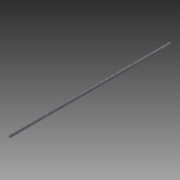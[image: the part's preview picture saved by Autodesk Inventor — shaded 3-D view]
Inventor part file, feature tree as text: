
AUTODESK INVENTOR PART (.ipt)
format: ipt  version: 2014 SP1 (Build 180222100, 222)  size: 1,561,088 bytes
history: native  units: in
note: dims shown in document units (in); Inventor stores cm internally (conversion verified against a paired STEP export)
features: sketch x3, extrude x1, helix x1, revolve x1, projected_geometry x1
ambient origin geometry x8: Origin, YZ Plane, XZ Plane, XY Plane, X Axis, Y Axis, Z Axis, Center Point
bodies: Solid1 (feature_tree)
feature tree (7):
  extrude  "Extrusion1"  Depth=0.126in TaperAngle=0.0deg
  helix  "Coil1"  [1 undecoded]
  revolve  "Revolution1"  Angle=30.0deg
  sketch  "Sketch1"  dims[d0=0.315in d1=19.685in d2=0.0in d3=0.126in]
  sketch  "Sketch2"  dims[d4=15.0deg d5=30.0deg]
  projected_geometry  "Projected Loop1"
  sketch  "Sketch3"  dims[d8=0.0394in d9=1.5748in d11=0.0787in d12=0.3937in d14=0.3937in d16=0.315in d17=20.0in d18=0.3937in d19=0.0in d20=90.0deg d21=90.0deg d22=0.0in d23=0.0in d24=150.0deg d26=0.0591in d27=150.0deg d28=90.0deg d29=0.0591in]
note: 1 required parameter value undecoded (feature->parameter linkage not recoverable at this tier; creation-order binding heuristic only, values carry confidence <= 0.55)
